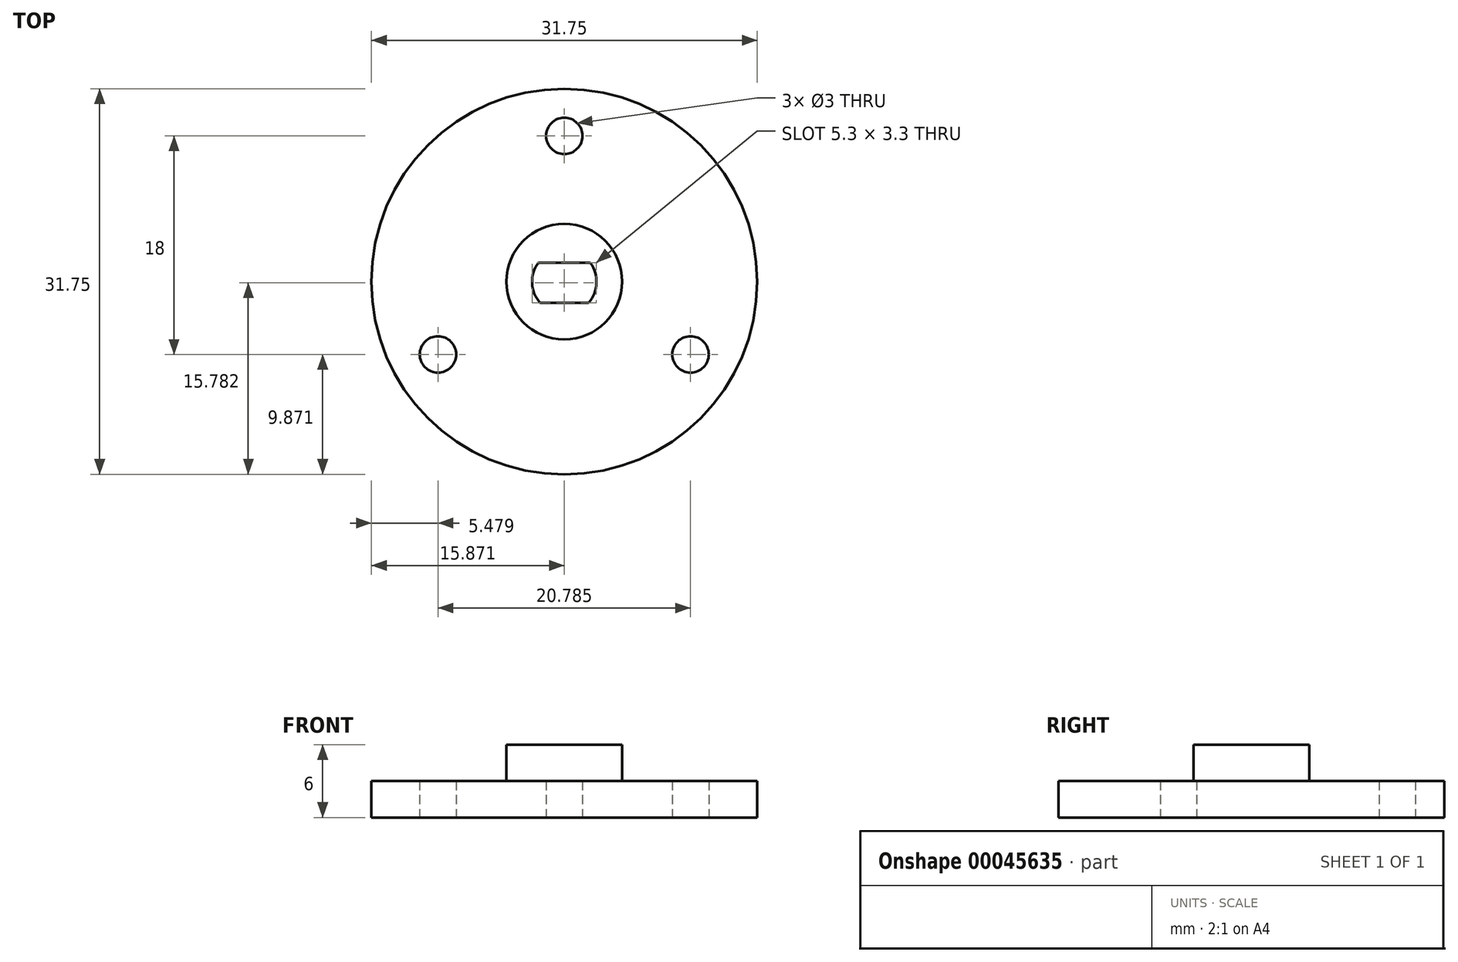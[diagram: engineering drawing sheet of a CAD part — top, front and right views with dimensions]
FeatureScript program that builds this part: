
annotation { "Feature Type Name" : "Feature", "Feature Type Description" : "" }
export const myFeature = defineFeature(function(context is Context, id is Id, definition is map)
    precondition{}
    {
        {
            var Q0;
            Q0=qCreatedBy(makeId("Top.planeOp"),FACE);
            var sketch = newSketch(context, id + "F0", { "sketchPlane" : qUnion([Q0])});
            skLineSegment(sketch, "E0.top", {"start": v(12.39, -114.3) * mm, "end": v(15.56, -114.3) * mm});
            skLineSegment(sketch, "E1.top", {"start": v(9.2, -142.88) * mm, "end": v(101.27, -142.88) * mm});
            skLineSegment(sketch, "E0.bottom", {"start": v(12.39, -111.13) * mm, "end": v(15.56, -111.13) * mm});
            skLineSegment(sketch, "E2", {"start": v(55.23, -98.43) * mm, "end": v(55.23, -142.88) * mm, "construction": true});
            skLineSegment(sketch, "E0.right", {"start": v(15.56, -111.13) * mm, "end": v(15.56, -114.3) * mm});
            skLineSegment(sketch, "E1.left", {"start": v(9.2, -107.95) * mm, "end": v(9.2, -142.88) * mm});
            skLineSegment(sketch, "E0.left", {"start": v(12.39, -111.13) * mm, "end": v(12.39, -114.3) * mm});
            skLineSegment(sketch, "E3.bottom", {"start": v(12.39, -117.48) * mm, "end": v(15.56, -117.48) * mm});
            skLineSegment(sketch, "E3.top", {"start": v(12.39, -120.65) * mm, "end": v(15.56, -120.65) * mm});
            skLineSegment(sketch, "E3.left", {"start": v(12.39, -117.48) * mm, "end": v(12.39, -120.65) * mm});
            skLineSegment(sketch, "E3.right", {"start": v(15.56, -117.48) * mm, "end": v(15.56, -120.65) * mm});
            skLineSegment(sketch, "E4.bottom", {"start": v(12.39, -123.83) * mm, "end": v(15.56, -123.83) * mm});
            skLineSegment(sketch, "E4.top", {"start": v(12.39, -127) * mm, "end": v(15.56, -127) * mm});
            skLineSegment(sketch, "E4.left", {"start": v(12.39, -123.83) * mm, "end": v(12.39, -127) * mm});
            skLineSegment(sketch, "E4.right", {"start": v(15.56, -123.83) * mm, "end": v(15.56, -127) * mm});
            skLineSegment(sketch, "E5", {"start": v(9.2, -107.95) * mm, "end": v(28.24, -98.43) * mm});
            skLineSegment(sketch, "E6.MirrorCS", {"start": v(98.07, -111.13) * mm, "end": v(94.9, -111.13) * mm});
            skLineSegment(sketch, "E7.MirrorCS", {"start": v(98.07, -117.48) * mm, "end": v(98.07, -120.65) * mm});
            skLineSegment(sketch, "E8.MirrorCS", {"start": v(98.07, -127) * mm, "end": v(94.9, -127) * mm});
            skLineSegment(sketch, "E9.MirrorCS", {"start": v(94.9, -117.48) * mm, "end": v(94.9, -120.65) * mm});
            skLineSegment(sketch, "E10.MirrorCS", {"start": v(98.07, -114.3) * mm, "end": v(94.9, -114.3) * mm});
            skLineSegment(sketch, "E11.MirrorCS", {"start": v(94.9, -111.13) * mm, "end": v(94.9, -114.3) * mm});
            skLineSegment(sketch, "E12.MirrorCS", {"start": v(101.27, -107.95) * mm, "end": v(82.22, -98.43) * mm});
            skLineSegment(sketch, "E13.MirrorCS", {"start": v(98.07, -111.13) * mm, "end": v(98.07, -114.3) * mm});
            skLineSegment(sketch, "E14.MirrorCS", {"start": v(98.07, -123.83) * mm, "end": v(94.9, -123.83) * mm});
            skLineSegment(sketch, "E15.MirrorCS", {"start": v(98.07, -117.48) * mm, "end": v(94.9, -117.48) * mm});
            skLineSegment(sketch, "E16.MirrorCS", {"start": v(94.9, -123.83) * mm, "end": v(94.9, -127) * mm});
            skLineSegment(sketch, "E17.MirrorCS", {"start": v(98.07, -120.65) * mm, "end": v(94.9, -120.65) * mm});
            skLineSegment(sketch, "E18.MirrorCS", {"start": v(98.07, -123.83) * mm, "end": v(98.07, -127) * mm});
            skLineSegment(sketch, "E19.MirrorCS", {"start": v(101.27, -107.95) * mm, "end": v(101.27, -142.88) * mm});
            skLineSegment(sketch, "E20.bottom", {"start": v(53.64, -98.43) * mm, "end": v(56.82, -98.43) * mm});
            skLineSegment(sketch, "E20.top", {"start": v(53.64, -101.6) * mm, "end": v(56.82, -101.6) * mm});
            skLineSegment(sketch, "E20.left", {"start": v(53.64, -98.43) * mm, "end": v(53.64, -101.6) * mm});
            skLineSegment(sketch, "E20.right", {"start": v(56.82, -98.43) * mm, "end": v(56.82, -101.6) * mm});
            skPoint(sketch, "E21", {"position": v(55.23, -98.43) * mm});
            skLineSegment(sketch, "E22.bottom", {"start": v(50.47, -101.6) * mm, "end": v(47.3, -101.6) * mm});
            skLineSegment(sketch, "E22.top", {"start": v(50.47, -98.43) * mm, "end": v(47.3, -98.43) * mm});
            skLineSegment(sketch, "E22.left", {"start": v(50.47, -101.6) * mm, "end": v(50.47, -98.43) * mm});
            skLineSegment(sketch, "E22.right", {"start": v(47.3, -101.6) * mm, "end": v(47.3, -98.43) * mm});
            skLineSegment(sketch, "E23.bottom", {"start": v(60, -101.6) * mm, "end": v(63.17, -101.6) * mm});
            skLineSegment(sketch, "E23.top", {"start": v(60, -98.43) * mm, "end": v(63.17, -98.43) * mm});
            skLineSegment(sketch, "E23.left", {"start": v(60, -101.6) * mm, "end": v(60, -98.43) * mm});
            skLineSegment(sketch, "E23.right", {"start": v(63.17, -101.6) * mm, "end": v(63.17, -98.43) * mm});
            skLineSegment(sketch, "E24", {"start": v(28.24, -98.43) * mm, "end": v(28.24, -95.25) * mm});
            skLineSegment(sketch, "E25", {"start": v(28.24, -95.25) * mm, "end": v(82.22, -95.25) * mm});
            skLineSegment(sketch, "E26", {"start": v(82.22, -95.25) * mm, "end": v(82.22, -98.43) * mm});
            skCircle(sketch, "E27", {"center": v(24.43, -106.68) * mm, "radius": 1.4 * mm});
            skCircle(sketch, "E28.0.1.0", {"center": v(24.43, -137.16) * mm, "radius": 1.4 * mm});
            skCircle(sketch, "E28.1.0.0", {"center": v(49.83, -106.68) * mm, "radius": 1.4 * mm});
            skCircle(sketch, "E28.1.1.0", {"center": v(49.83, -137.16) * mm, "radius": 1.4 * mm});
            skLineSegment(sketch, "E28.direction1", {"start": v(24.43, -106.68) * mm, "end": v(49.83, -106.68) * mm, "construction": true});
            skLineSegment(sketch, "E28.direction2", {"start": v(24.43, -106.68) * mm, "end": v(24.43, -137.16) * mm, "construction": true});
            skCircle(sketch, "E29.MirrorC", {"center": v(60.63, -137.16) * mm, "radius": 1.4 * mm});
            skCircle(sketch, "E30.MirrorC", {"center": v(60.63, -106.68) * mm, "radius": 1.4 * mm});
            skCircle(sketch, "E31.MirrorC", {"center": v(86.03, -106.68) * mm, "radius": 1.4 * mm});
            skCircle(sketch, "E32.MirrorC", {"center": v(86.03, -137.16) * mm, "radius": 1.4 * mm});
            skSolve(sketch);
        }
        {
            var Q0;
            Q0=qCreatedBy(makeId("Top.planeOp"),FACE);
            var sketch = newSketch(context, id + "F1", { "sketchPlane" : qUnion([Q0])});
            skLineSegment(sketch, "E33.top", {"start": v(31.26, -167.33) * mm, "end": v(35.26, -167.33) * mm});
            skLineSegment(sketch, "E33.bottom", {"start": v(31.12, -164.03) * mm, "end": v(35.4, -164.03) * mm});
            skCircle(sketch, "E34", {"center": v(33.26, -165.59) * mm, "radius": 4.76 * mm});
            skCircle(sketch, "E35", {"center": v(33.26, -165.59) * mm, "radius": 15.88 * mm});
            skLineSegment(sketch, "E36", {"start": v(33.26, -165.59) * mm, "end": v(33.26, -153.59) * mm, "construction": true});
            skCircle(sketch, "E37", {"center": v(33.26, -153.59) * mm, "radius": 1.5 * mm});
            skCircle(sketch, "E38.1.0", {"center": v(22.87, -171.59) * mm, "radius": 1.5 * mm});
            skCircle(sketch, "E38.2.0", {"center": v(43.65, -171.59) * mm, "radius": 1.5 * mm});
            skCircle(sketch, "E39", {"center": v(33.26, -165.59) * mm, "radius": 2.65 * mm});
            skSolve(sketch);
        }
        {
            var Q0;
            {var subQ0=sQuery(id+"F1.wireOp",EDGE,"E33.bottom");Q0=makeQuery(id+"F1.imprint","IMPRINT",FACE,{"disambiguationData":[TD([[makeQuery(id+"F1.imprint","IMPRINT",EDGE,{"derivedFrom":subQ0}),1.0]])]});}
            var Q1;
            {var subQ0=sQuery(id+"F1.wireOp",EDGE,"E33.top");Q1=makeQuery(id+"F1.imprint","IMPRINT",FACE,{"disambiguationData":[TD([[makeQuery(id+"F1.imprint","IMPRINT",EDGE,{"derivedFrom":subQ0}),-1.0]])]});}
            var Q2;
            Q2=makeQuery(id+"F1.imprint","IMPRINT",FACE,{"disambiguationData":[TD([[makeQuery(id+"F1.imprint","IMPRINT",EDGE,{"derivedFrom":sQuery(id+"F1.wireOp",EDGE,"E34")}),1.0]])]});
            extrude(context, id + "F2", {"entities" : qUnion([Q0, Q1, Q2]), "depth" : 6 * mm});
        }
        {
            var Q0;
            Q0=makeQuery(id+"F1.imprint","IMPRINT",FACE,{"disambiguationData":[TD([[makeQuery(id+"F1.imprint","IMPRINT",EDGE,{"derivedFrom":sQuery(id+"F1.wireOp",EDGE,"E34")}),-1.0]])]});
            extrude(context, id + "F3", {"entities" : qUnion([Q0]), "operationType" : NewBodyOperationType.ADD, "depth" : 3 * mm});
        }
    });
